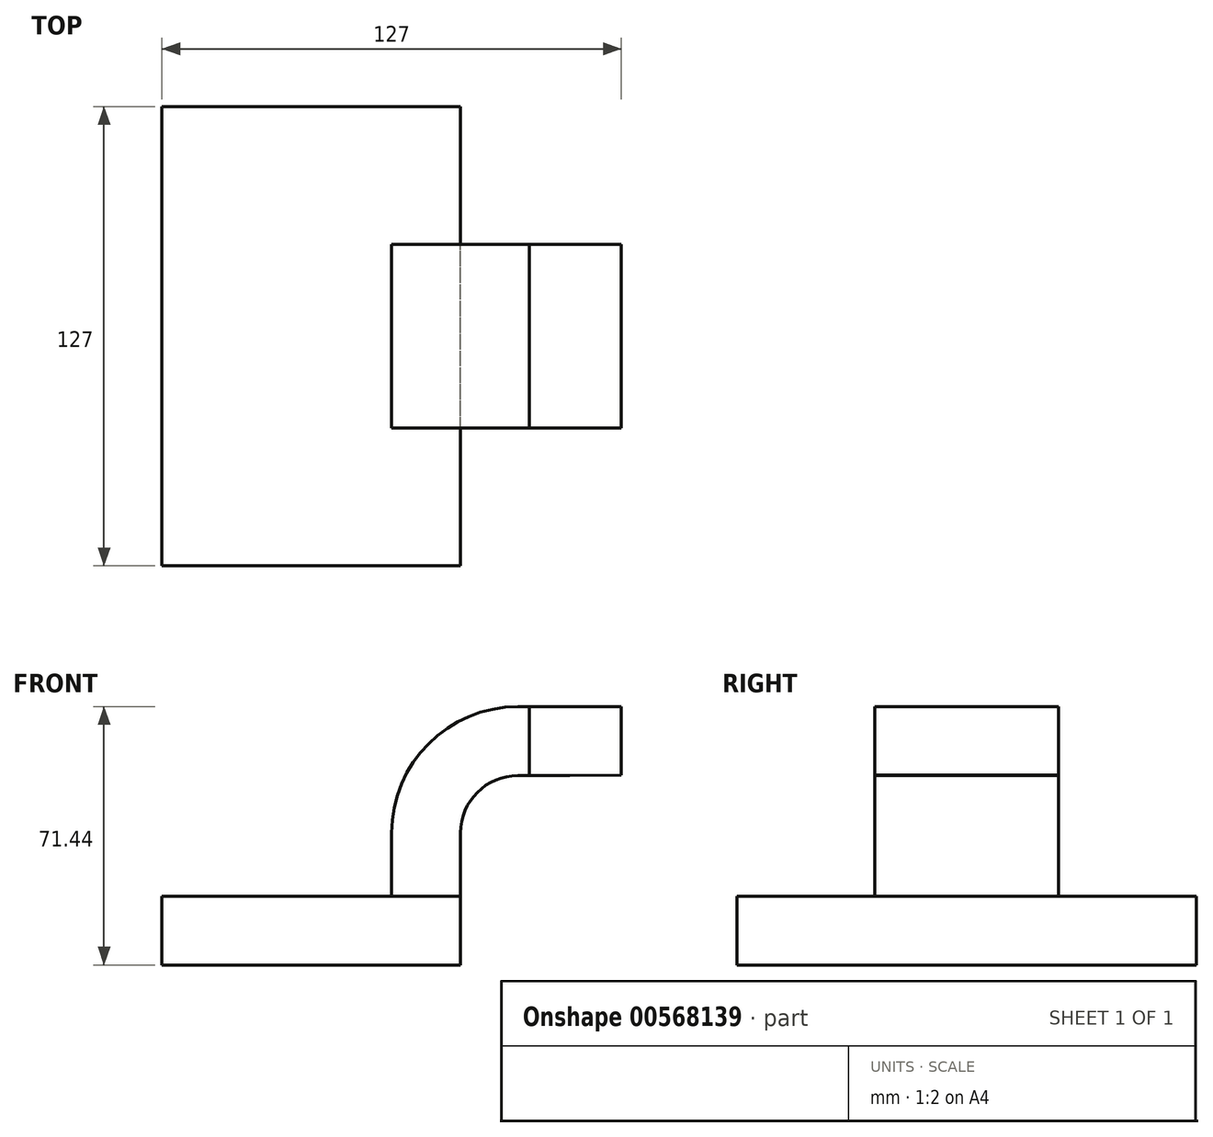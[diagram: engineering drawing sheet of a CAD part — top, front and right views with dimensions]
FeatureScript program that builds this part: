
annotation { "Feature Type Name" : "Feature", "Feature Type Description" : "" }
export const myFeature = defineFeature(function(context is Context, id is Id, definition is map)
    precondition{}
    {
        {
            var Q0;
            Q0=qCreatedBy(makeId("Front.planeOp"),FACE);
            var sketch = newSketch(context, id + "F0", { "sketchPlane" : qUnion([Q0])});
            skLineSegment(sketch, "E0.bottom", {"start": v(41.27, 9.53) * mm, "end": v(-41.28, 9.53) * mm});
            skLineSegment(sketch, "E0.top", {"start": v(41.28, -9.52) * mm, "end": v(-41.27, -9.52) * mm});
            skLineSegment(sketch, "E0.left", {"start": v(41.28, 9.53) * mm, "end": v(41.28, -9.52) * mm});
            skLineSegment(sketch, "E0.right", {"start": v(-41.28, 9.53) * mm, "end": v(-41.27, -9.52) * mm});
            skPoint(sketch, "E0.middle", {"position": v(0, 0) * mm});
            skLineSegment(sketch, "E1.bottom", {"start": v(111.12, 38.1) * mm, "end": v(60.32, 38.1) * mm});
            skLineSegment(sketch, "E1.top", {"start": v(111.12, 66.68) * mm, "end": v(60.32, 66.68) * mm});
            skLineSegment(sketch, "E1.left", {"start": v(111.12, 38.1) * mm, "end": v(111.12, 66.68) * mm});
            skLineSegment(sketch, "E1.right", {"start": v(60.32, 38.1) * mm, "end": v(60.32, 66.68) * mm});
            skPoint(sketch, "E1.middle", {"position": v(85.72, 52.39) * mm});
            skLineSegment(sketch, "E2", {"start": v(41.27, 9.53) * mm, "end": v(41.27, 26.99) * mm});
            skArc(sketch, "E3", {"start": v(41.27, 26.99) * mm, "mid": v(45.92, 38.21) * mm, "end": v(57.15, 42.86) * mm});
            skLineSegment(sketch, "E4", {"start": v(57.15, 42.86) * mm, "end": v(71.48, 42.86) * mm});
            skArc(sketch, "E5.0", {"start": v(47.62, 26.99) * mm, "mid": v(50.41, 33.72) * mm, "end": v(57.15, 36.51) * mm});
            skLineSegment(sketch, "E5.1", {"start": v(47.62, 9.53) * mm, "end": v(47.62, 26.99) * mm});
            skLineSegment(sketch, "E6.0", {"start": v(57.15, 61.91) * mm, "end": v(71.48, 61.91) * mm});
            skArc(sketch, "E6.1", {"start": v(22.22, 26.99) * mm, "mid": v(32.45, 51.68) * mm, "end": v(57.15, 61.91) * mm});
            skLineSegment(sketch, "E6.2", {"start": v(22.22, 9.53) * mm, "end": v(22.22, 26.99) * mm});
            skLineSegment(sketch, "E7", {"start": v(71.48, 61.91) * mm, "end": v(85.72, 61.91) * mm});
            skPoint(sketch, "E7.endSnap0", {"position": v(85.72, 66.68) * mm});
            skLineSegment(sketch, "E8", {"start": v(85.72, 61.91) * mm, "end": v(85.72, 42.95) * mm});
            skLineSegment(sketch, "E9", {"start": v(85.72, 42.95) * mm, "end": v(71.48, 42.86) * mm});
            skLineSegment(sketch, "E10", {"start": v(85.72, 66.68) * mm, "end": v(85.72, 61.91) * mm});
            skFitSpline(sketch, "E11", {"points": [v(-41.28, 9.53) * mm, v(60.32, 61.91) * mm], "startDerivative": vector(2.2, 137.14) * mm, "endDerivative": vector(131.1, -2.29) * mm});
            skSolve(sketch);
        }
        {
            var Q0;
            Q0=makeQuery(id+"F0.imprint","IMPRINT",FACE,{"disambiguationData":[TD([[makeQuery(id+"F0.imprint","IMPRINT",EDGE,{"derivedFrom":sQuery(id+"F0.wireOp",EDGE,"E0.top")}),-1.0]])]});
            extrude(context, id + "F1", {"entities" : qUnion([Q0]), "endBound" : BoundingType.SYMMETRIC, "depth" : 127 * mm, "offsetDistance" : 25.4 * mm});
        }
        {
            var Q0;
            {var subQ1=sQuery(id+"F0.wireOp",EDGE,"E2");Q0=makeQuery(id+"F0.imprint","IMPRINT",FACE,{"disambiguationData":[TD([[makeQuery(id+"F0.imprint","IMPRINT",EDGE,{"derivedFrom":subQ1}),1.0]])]});}
            extrude(context, id + "F2", {"entities" : qUnion([Q0]), "operationType" : NewBodyOperationType.ADD, "endBound" : BoundingType.SYMMETRIC, "depth" : 50.8 * mm, "offsetDistance" : 25.4 * mm});
        }
        {
            var Q0;
            {var subQ0=sQuery(id+"F0.wireOp",EDGE,"E7");Q0=makeQuery(id+"F0.imprint","IMPRINT",FACE,{"disambiguationData":[TD([[makeQuery(id+"F0.imprint","IMPRINT",EDGE,{"derivedFrom":subQ0}),-1.0]])]});}
            extrude(context, id + "F3", {"entities" : qUnion([Q0]), "operationType" : NewBodyOperationType.ADD, "endBound" : BoundingType.SYMMETRIC, "depth" : 50.8 * mm, "offsetDistance" : 25.4 * mm});
        }
        {
            var Q0;
            {var subQ1=sQuery(id+"F0.wireOp",EDGE,"E6.1");Q0=makeQuery(id+"F0.imprint","IMPRINT",FACE,{"disambiguationData":[TD([[makeQuery(id+"F0.imprint","IMPRINT",EDGE,{"derivedFrom":subQ1}),1.0]])]});}
            extrude(context, id + "F4", {"entities" : qUnion([Q0]), "endBound" : BoundingType.SYMMETRIC, "depth" : 50.8 * mm, "offsetDistance" : 25.4 * mm});
        }
    });
